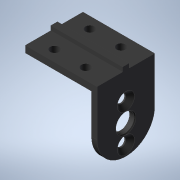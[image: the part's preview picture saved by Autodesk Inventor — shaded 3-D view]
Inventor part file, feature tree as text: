
AUTODESK INVENTOR PART (.ipt)
format: ipt  version: 2021 (Build 250183000, 183)  size: 207,360 bytes
history: native  units: mm
features: extrude x4, other x3, chamfer x2, sketch x2, fillet x1
ambient origin geometry x8: Origin, YZ Plane, XZ Plane, XY Plane, X Axis, Y Axis, Z Axis, Center Point
bodies: Body1 (feature_tree)
feature tree (12):
  other  "00_Mastersketch.ipt"
  extrude  "Extrusion2"  Depth=26.3mm
  extrude  "Extrusion3"  TaperAngle=0.0deg  [1 undecoded]
  extrude  "Extrusion4"  Depth=3.0mm
  fillet  "Rundung2"  Radius=3.9mm
  chamfer  "Fase2"  [1 undecoded]
  chamfer  "Fase3"  Distance=2.0mm Angle=45.0deg
  extrude  "Extrusion5"  Depth=2.0mm TaperAngle=45.0deg
  other  "01_caseBottom"
  other  "06_motorHolderSketch"
  sketch  "Skizze6"  dims[d0=10.0mm d36=26.3mm]
  sketch  "Skizze7"  dims[d37=0.0mm d38=0.0mm d39=0.0mm d40=8.4mm d41=3.9mm d42=0.0mm d43=0.0mm d44=2.0mm d45=2.0mm d46=45.0deg d47=0.4mm d48=2.0mm d49=45.0deg d50=0.3mm d51=2.0mm d52=3.0mm d53=0.0mm]
note: 2 required parameter values undecoded (feature->parameter linkage not recoverable at this tier; creation-order binding heuristic only, values carry confidence <= 0.55)
